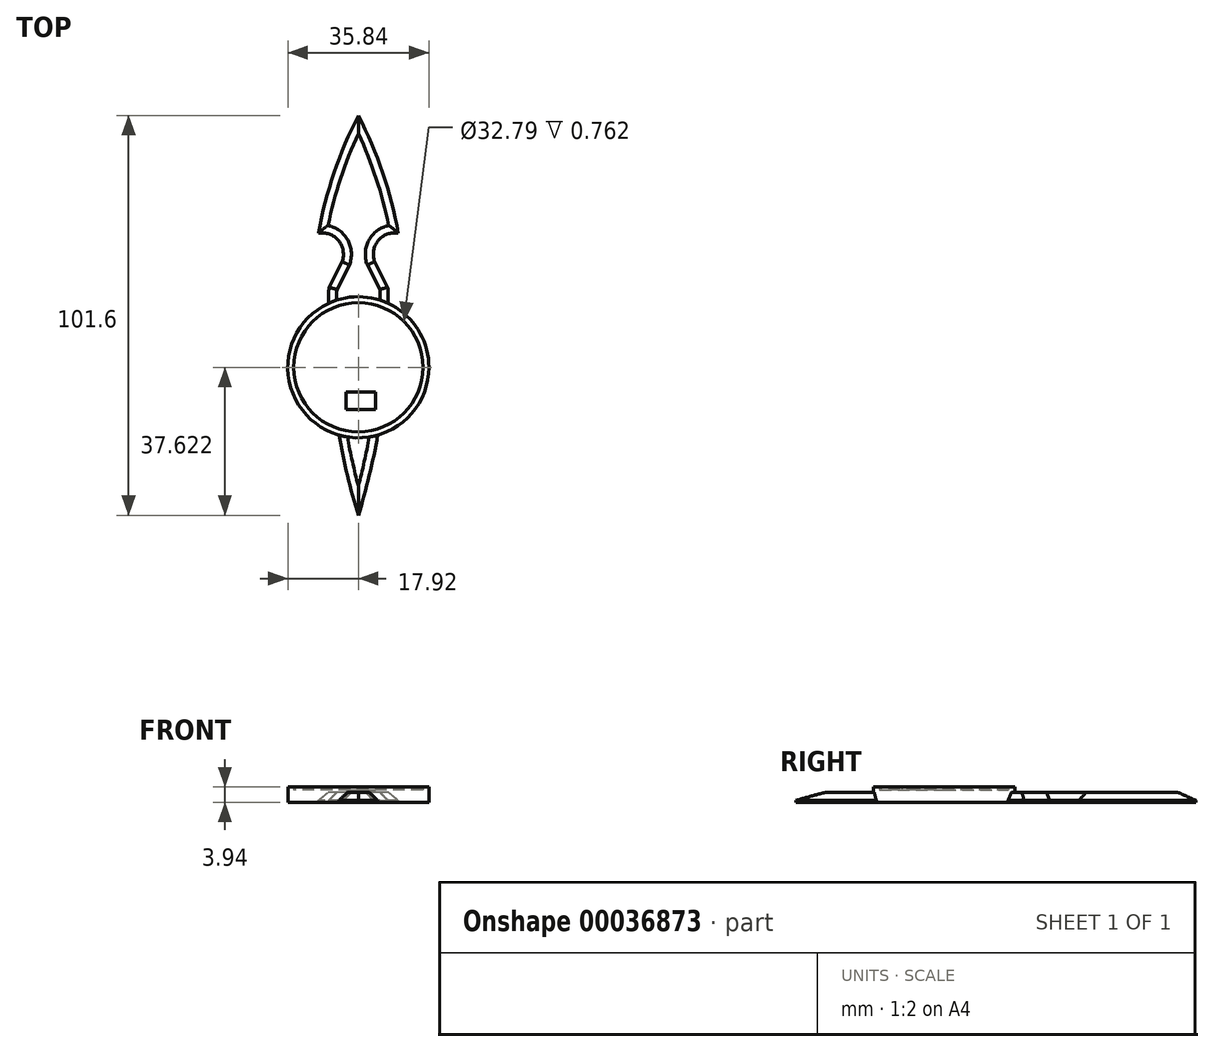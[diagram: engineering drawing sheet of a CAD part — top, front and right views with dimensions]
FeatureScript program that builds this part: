
annotation { "Feature Type Name" : "Feature", "Feature Type Description" : "" }
export const myFeature = defineFeature(function(context is Context, id is Id, definition is map)
    precondition{}
    {
        {
            var Q0;
            Q0=qCreatedBy(makeId("Top.planeOp"),FACE);
            var sketch = newSketch(context, id + "F0", { "sketchPlane" : qUnion([Q0])});
            skArc(sketch, "E0", {"start": v(0, -50.8) * mm, "mid": v(6.2, -22.15) * mm, "end": v(7.47, 7.13) * mm});
            skLineSegment(sketch, "E1", {"start": v(0, 50.8) * mm, "end": v(0, -50.8) * mm, "construction": true});
            skArc(sketch, "E2.MirrorCS", {"start": v(0, -50.8) * mm, "mid": v(-6.2, -22.15) * mm, "end": v(-7.47, 7.13) * mm});
            skArc(sketch, "E3", {"start": v(0, 50.8) * mm, "mid": v(-6.17, 36.23) * mm, "end": v(-10.14, 20.91) * mm});
            skArc(sketch, "E4", {"start": v(-4.13, 13.65) * mm, "mid": v(-5.05, 19) * mm, "end": v(-10.14, 20.91) * mm});
            skLineSegment(sketch, "E5", {"start": v(-4.13, 13.65) * mm, "end": v(-7.47, 7.13) * mm});
            skArc(sketch, "E6.trimOffspring", {"start": v(-6.44, 20.2) * mm, "mid": v(-3.91, 35.65) * mm, "end": v(0, 50.8) * mm});
            skLineSegment(sketch, "E7.MirrorCS", {"start": v(4.13, 13.65) * mm, "end": v(7.47, 7.13) * mm});
            skArc(sketch, "E8.MirrorCS", {"start": v(4.13, 13.65) * mm, "mid": v(5.05, 19) * mm, "end": v(10.14, 20.91) * mm});
            skArc(sketch, "E9.MirrorCS", {"start": v(0, 50.8) * mm, "mid": v(6.17, 36.23) * mm, "end": v(10.14, 20.91) * mm});
            skArc(sketch, "E10.trimOffspring", {"start": v(6.44, 20.2) * mm, "mid": v(3.91, 35.65) * mm, "end": v(0, 50.8) * mm});
            skSolve(sketch);
        }
        {
            var Q0;
            Q0 = qSketchRegion(id + "F0", true);
            extrude(context, id + "F1", {"entities" : qUnion([Q0]), "depth" : 2.54 * mm});
        }
        {
            var Q0;
            Q0=qCreatedBy(makeId("Top.planeOp"),FACE);
            var sketch = newSketch(context, id + "F2", { "sketchPlane" : qUnion([Q0])});
            skCircle(sketch, "E11", {"center": v(0, -13.18) * mm, "radius": 17.92 * mm});
            skSolve(sketch);
        }
        {
            var Q0;
            Q0 = qSketchRegion(id + "F2", true);
            extrude(context, id + "F3", {"entities" : qUnion([Q0]), "operationType" : NewBodyOperationType.ADD, "depth" : 3.17 * mm});
        }
        {
            var Q0;
            Q0=makeQuery(id+"F3.opExtrude","CAP_FACE",FACE,{"disambiguationData":[OSD([sQuery(id+"F2.wireOp",EDGE,"E11")])],"isStart":false});
            var sketch = newSketch(context, id + "F4", { "sketchPlane" : qUnion([Q0])});
            skCircle(sketch, "E12.0", {"center": v(0, -13.18) * mm, "radius": 17.92 * mm});
            skCircle(sketch, "E13.0", {"center": v(0, -13.18) * mm, "radius": 16.4 * mm});
            skSolve(sketch);
        }
        {
            var Q0;
            Q0 = qSketchRegion(id + "F4", true);
            extrude(context, id + "F5", {"entities" : qUnion([Q0]), "operationType" : NewBodyOperationType.ADD, "depth" : 0.76 * mm});
        }
        {
            var Q0;
            Q0=makeQuery(id+"F3.opExtrude","CAP_FACE",FACE,{"disambiguationData":[OSD([sQuery(id+"F2.wireOp",EDGE,"E11")])],"isStart":false});
            var sketch = newSketch(context, id + "F6", { "sketchPlane" : qUnion([Q0])});
            skLineSegment(sketch, "E14.bottom", {"start": v(-3.13, -19.4) * mm, "end": v(4.38, -19.4) * mm});
            skLineSegment(sketch, "E14.top", {"start": v(-3.13, -23.92) * mm, "end": v(4.38, -23.92) * mm});
            skLineSegment(sketch, "E14.left", {"start": v(-3.13, -19.4) * mm, "end": v(-3.13, -23.92) * mm});
            skLineSegment(sketch, "E14.right", {"start": v(4.38, -19.4) * mm, "end": v(4.38, -23.92) * mm});
            skSolve(sketch);
        }
        {
            var Q0;
            Q0 = qSketchRegion(id + "F6", true);
            extrude(context, id + "F7", {"entities" : qUnion([Q0]), "operationType" : NewBodyOperationType.ADD, "depth" : 0.76 * mm});
        }
        {
            var Q0;
            Q0=makeQuery(id+"F1.opExtrude","CAP_EDGE",EDGE,{"disambiguationData":[OSD([sQuery(id+"F0.wireOp",EDGE,"E3")])],"isStart":false});
            var Q1;
            Q1=makeQuery(id+"F1.opExtrude","CAP_EDGE",EDGE,{"disambiguationData":[OSD([sQuery(id+"F0.wireOp",EDGE,"E9.MirrorCS")])],"isStart":false});
            var Q2;
            Q2=makeQuery(id+"F1.opExtrude","CAP_EDGE",EDGE,{"disambiguationData":[OSD([sQuery(id+"F0.wireOp",EDGE,"E4")])],"isStart":false});
            var Q3;
            Q3=makeQuery(id+"F1.opExtrude","CAP_EDGE",EDGE,{"disambiguationData":[OSD([sQuery(id+"F0.wireOp",EDGE,"E8.MirrorCS")])],"isStart":false});
            var Q4;
            Q4=makeQuery(id+"F1.opExtrude","CAP_EDGE",EDGE,{"disambiguationData":[OSD([sQuery(id+"F0.wireOp",EDGE,"E7.MirrorCS")])],"isStart":false});
            var Q5;
            Q5=makeQuery(id+"F1.opExtrude","CAP_EDGE",EDGE,{"disambiguationData":[OSD([sQuery(id+"F0.wireOp",EDGE,"E5")])],"isStart":false});
            var Q6;
            {var subQ0=sQuery(id+"F0.wireOp",EDGE,"E2.MirrorCS");var subQ1=sQuery(id+"F0.wireOp",EDGE,"E5");Q6=makeQuery(id+"F3.boolean.opBoolean","SPLIT",EDGE,{"disambiguationData":[TD([makeQuery(id+"F1.opExtrude","SWEPT_FACE",FACE,{"disambiguationData":[OSD([subQ1])]})])],"derivedFrom":makeQuery(id+"F1.opExtrude","CAP_EDGE",EDGE,{"disambiguationData":[OSD([subQ0])],"isStart":false})});}
            var Q7;
            {var subQ0=sQuery(id+"F0.wireOp",EDGE,"E0");var subQ1=sQuery(id+"F0.wireOp",EDGE,"E7.MirrorCS");Q7=makeQuery(id+"F3.boolean.opBoolean","SPLIT",EDGE,{"disambiguationData":[TD([makeQuery(id+"F1.opExtrude","SWEPT_FACE",FACE,{"disambiguationData":[OSD([subQ1])]})])],"derivedFrom":makeQuery(id+"F1.opExtrude","CAP_EDGE",EDGE,{"disambiguationData":[OSD([subQ0])],"isStart":false})});}
            var Q8;
            {var subQ0=sQuery(id+"F0.wireOp",EDGE,"E2.MirrorCS");var subQ1=sQuery(id+"F0.wireOp",EDGE,"E0");Q8=makeQuery(id+"F3.boolean.opBoolean","SPLIT",EDGE,{"disambiguationData":[TD([makeQuery(id+"F1.opExtrude","SWEPT_FACE",FACE,{"disambiguationData":[OSD([subQ1])]})])],"derivedFrom":makeQuery(id+"F1.opExtrude","CAP_EDGE",EDGE,{"disambiguationData":[OSD([subQ0])],"isStart":false})});}
            var Q9;
            {var subQ0=sQuery(id+"F0.wireOp",EDGE,"E0");var subQ1=sQuery(id+"F0.wireOp",EDGE,"E2.MirrorCS");Q9=makeQuery(id+"F3.boolean.opBoolean","SPLIT",EDGE,{"disambiguationData":[TD([makeQuery(id+"F1.opExtrude","SWEPT_FACE",FACE,{"disambiguationData":[OSD([subQ1])]})])],"derivedFrom":makeQuery(id+"F1.opExtrude","CAP_EDGE",EDGE,{"disambiguationData":[OSD([subQ0])],"isStart":false})});}
            chamfer(context, id + "F8", {"entities" : qUnion([Q0, Q1, Q2, Q3, Q4, Q5, Q6, Q7, Q8, Q9]), "width" : 2.03 * mm, "tangentPropagation" : true});
        }
    });
